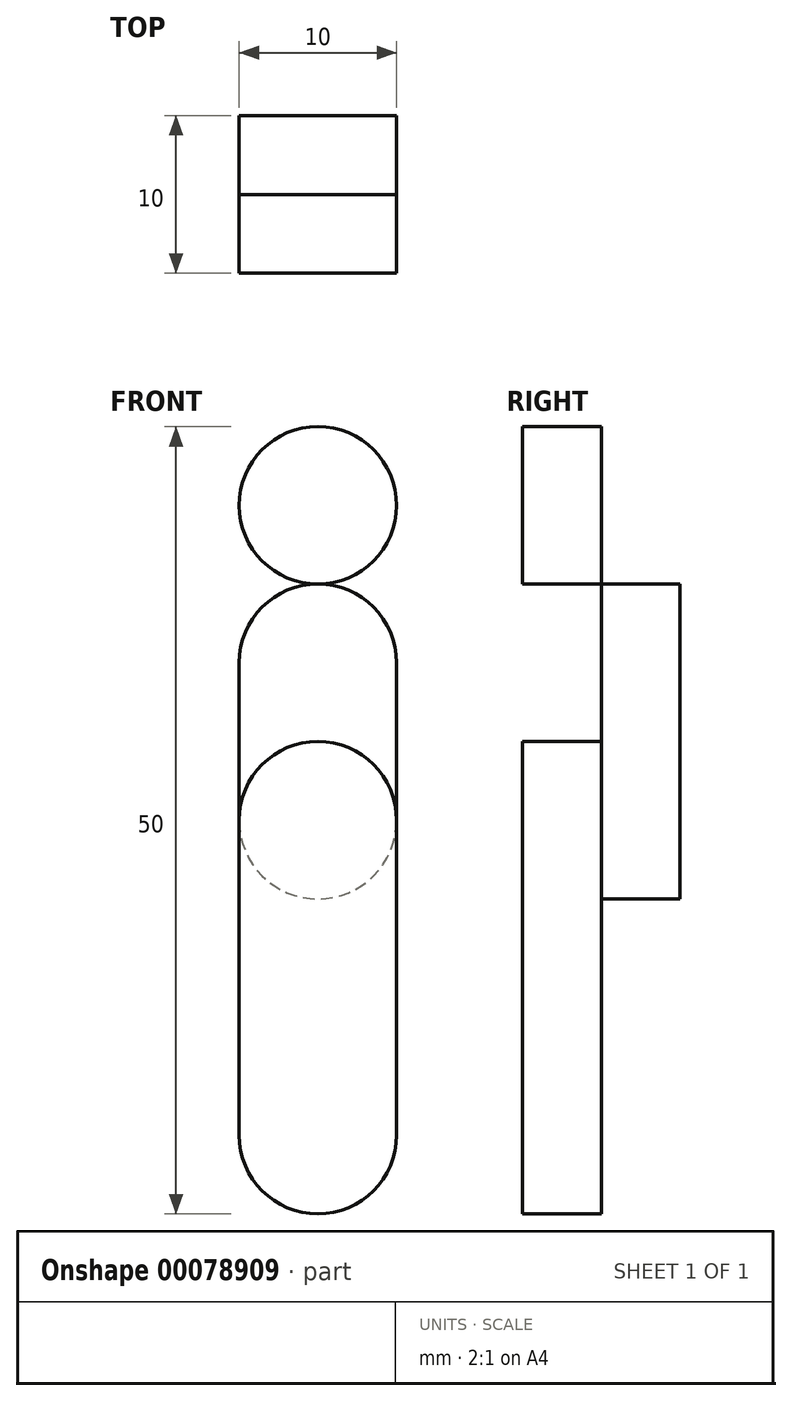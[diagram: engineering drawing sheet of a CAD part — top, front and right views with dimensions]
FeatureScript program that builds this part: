
annotation { "Feature Type Name" : "Feature", "Feature Type Description" : "" }
export const myFeature = defineFeature(function(context is Context, id is Id, definition is map)
    precondition{}
    {
        {
            var Q0;
            Q0=qCreatedBy(makeId("Front.planeOp"),FACE);
            var sketch = newSketch(context, id + "F0", { "sketchPlane" : qUnion([Q0])});
            skArc(sketch, "E0", {"start": v(10, 0) * mm, "mid": v(5, 5) * mm, "end": v(0, 0) * mm});
            skLineSegment(sketch, "E1", {"start": v(10, 0) * mm, "end": v(10, -20) * mm});
            skLineSegment(sketch, "E2", {"start": v(0, 0) * mm, "end": v(0, -20) * mm});
            skArc(sketch, "E3", {"start": v(0, -20) * mm, "mid": v(5, -25) * mm, "end": v(10, -20) * mm});
            skCircle(sketch, "E4", {"center": v(5, -10) * mm, "radius": 5 * mm});
            skLineSegment(sketch, "E5", {"start": v(0, 0) * mm, "end": v(10, -20) * mm, "construction": true});
            skLineSegment(sketch, "E6", {"start": v(10, 0) * mm, "end": v(0, -20) * mm, "construction": true});
            skCircle(sketch, "E7", {"center": v(5, 0) * mm, "radius": 5 * mm});
            skCircle(sketch, "E8", {"center": v(5, -20) * mm, "radius": 5 * mm});
            skArc(sketch, "E9", {"start": v(10, 30) * mm, "mid": v(5, 35) * mm, "end": v(0, 30) * mm});
            skLineSegment(sketch, "E10", {"start": v(10, 30) * mm, "end": v(10, 10) * mm});
            skLineSegment(sketch, "E11", {"start": v(0, 30) * mm, "end": v(0, 10) * mm});
            skArc(sketch, "E12", {"start": v(0, 10) * mm, "mid": v(5, 5) * mm, "end": v(10, 10) * mm});
            skCircle(sketch, "E13", {"center": v(5, 20) * mm, "radius": 5 * mm});
            skLineSegment(sketch, "E14", {"start": v(0, 30) * mm, "end": v(10, 10) * mm, "construction": true});
            skLineSegment(sketch, "E15", {"start": v(10, 30) * mm, "end": v(0, 10) * mm, "construction": true});
            skCircle(sketch, "E16", {"center": v(5, 30) * mm, "radius": 5 * mm});
            skCircle(sketch, "E17", {"center": v(5, 10) * mm, "radius": 5 * mm});
            skLineSegment(sketch, "E18", {"start": v(0, 10) * mm, "end": v(0, 0) * mm});
            skLineSegment(sketch, "E19", {"start": v(10, 0) * mm, "end": v(10, 10) * mm});
            skSolve(sketch);
        }
        {
            var Q0;
            {var subQ0=sQuery(id+"F0.wireOp",EDGE,"E7");var subQ2=makeQuery(id+"F0.imprint","INTERSECT",VERTEX,{"derivedFrom":[subQ0,sQuery(id+"F0.wireOp",EDGE,"E17")]});Q0=makeQuery(id+"F0.imprint","IMPRINT",FACE,{"disambiguationData":[TD([[makeQuery(id+"F0.imprint","IMPRINT",EDGE,{"disambiguationData":[TD([[subQ2,1.0]])],"derivedFrom":subQ0}),1.0]])]});}
            var Q1;
            {var subQ1=sQuery(id+"F0.wireOp",EDGE,"E2");var subQ3=sQuery(id+"F0.wireOp",EDGE,"E4");var subQ4=makeQuery(id+"F0.imprint","INTERSECT",VERTEX,{"derivedFrom":[subQ1,subQ3]});Q1=makeQuery(id+"F0.imprint","IMPRINT",FACE,{"disambiguationData":[TD([[makeQuery(id+"F0.imprint","IMPRINT",EDGE,{"disambiguationData":[TD([[subQ4,1.0]])],"derivedFrom":subQ3}),-1.0]])]});}
            var Q2;
            {var subQ0=sQuery(id+"F0.wireOp",EDGE,"E4");var subQ1=makeQuery(id+"F0.imprint","INTERSECT",VERTEX,{"derivedFrom":[sQuery(id+"F0.wireOp",EDGE,"E1"),subQ0]});Q2=makeQuery(id+"F0.imprint","IMPRINT",FACE,{"disambiguationData":[TD([[makeQuery(id+"F0.imprint","IMPRINT",EDGE,{"disambiguationData":[TD([[subQ1,-1.0]])],"derivedFrom":subQ0}),1.0]])]});}
            var Q3;
            {var subQ0=sQuery(id+"F0.wireOp",EDGE,"E8");var subQ1=sQuery(id+"F0.wireOp",EDGE,"E2");var subQ2=makeQuery(id+"F0.imprint","INTERSECT",VERTEX,{"derivedFrom":[subQ1,subQ0]});Q3=makeQuery(id+"F0.imprint","IMPRINT",FACE,{"disambiguationData":[TD([[makeQuery(id+"F0.imprint","IMPRINT",EDGE,{"disambiguationData":[TD([[subQ2,1.0]])],"derivedFrom":subQ1}),1.0]])]});}
            var Q4;
            {var subQ0=sQuery(id+"F0.wireOp",EDGE,"E8");var subQ1=makeQuery(id+"F0.imprint","INTERSECT",VERTEX,{"derivedFrom":[sQuery(id+"F0.wireOp",EDGE,"E1"),subQ0]});Q4=makeQuery(id+"F0.imprint","IMPRINT",FACE,{"disambiguationData":[TD([[makeQuery(id+"F0.imprint","IMPRINT",EDGE,{"disambiguationData":[TD([[subQ1,-1.0]])],"derivedFrom":subQ0}),1.0]])]});}
            var Q5;
            {var subQ0=sQuery(id+"F0.wireOp",EDGE,"E8");var subQ1=sQuery(id+"F0.wireOp",EDGE,"E1");var subQ2=makeQuery(id+"F0.imprint","INTERSECT",VERTEX,{"derivedFrom":[subQ1,subQ0]});Q5=makeQuery(id+"F0.imprint","IMPRINT",FACE,{"disambiguationData":[TD([[makeQuery(id+"F0.imprint","IMPRINT",EDGE,{"disambiguationData":[TD([[subQ2,1.0]])],"derivedFrom":subQ1}),-1.0]])]});}
            var Q6;
            {var subQ1=sQuery(id+"F0.wireOp",EDGE,"E1");var subQ3=sQuery(id+"F0.wireOp",EDGE,"E4");var subQ4=makeQuery(id+"F0.imprint","INTERSECT",VERTEX,{"derivedFrom":[subQ1,subQ3]});Q6=makeQuery(id+"F0.imprint","IMPRINT",FACE,{"disambiguationData":[TD([[makeQuery(id+"F0.imprint","IMPRINT",EDGE,{"disambiguationData":[TD([[subQ4,-1.0]])],"derivedFrom":subQ3}),-1.0]])]});}
            extrude(context, id + "F1", {"entities" : qUnion([Q0, Q1, Q2, Q3, Q4, Q5, Q6]), "depth" : 5 * mm});
        }
        {
            var Q0;
            {var subQ0=sQuery(id+"F0.wireOp",EDGE,"E7");var subQ2=makeQuery(id+"F0.imprint","INTERSECT",VERTEX,{"derivedFrom":[subQ0,sQuery(id+"F0.wireOp",EDGE,"E17")]});Q0=makeQuery(id+"F0.imprint","IMPRINT",FACE,{"disambiguationData":[TD([[makeQuery(id+"F0.imprint","IMPRINT",EDGE,{"disambiguationData":[TD([[subQ2,1.0]])],"derivedFrom":subQ0}),1.0]])]});}
            var Q1;
            {var subQ0=sQuery(id+"F0.wireOp",EDGE,"E18");Q1=makeQuery(id+"F0.imprint","IMPRINT",FACE,{"disambiguationData":[TD([[makeQuery(id+"F0.imprint","IMPRINT",EDGE,{"derivedFrom":subQ0}),1.0]])]});}
            var Q2;
            {var subQ0=sQuery(id+"F0.wireOp",EDGE,"E19");Q2=makeQuery(id+"F0.imprint","IMPRINT",FACE,{"disambiguationData":[TD([[makeQuery(id+"F0.imprint","IMPRINT",EDGE,{"derivedFrom":subQ0}),1.0]])]});}
            var Q3;
            {var subQ0=sQuery(id+"F0.wireOp",EDGE,"E17");var subQ2=makeQuery(id+"F0.imprint","INTERSECT",VERTEX,{"derivedFrom":[sQuery(id+"F0.wireOp",EDGE,"E13"),subQ0]});Q3=makeQuery(id+"F0.imprint","IMPRINT",FACE,{"disambiguationData":[TD([[makeQuery(id+"F0.imprint","IMPRINT",EDGE,{"disambiguationData":[TD([[subQ2,1.0]])],"derivedFrom":subQ0}),1.0]])]});}
            extrude(context, id + "F2", {"entities" : qUnion([Q0, Q1, Q2, Q3]), "oppositeDirection" : true, "depth" : 5 * mm});
        }
        {
            var Q0;
            {var subQ0=sQuery(id+"F0.wireOp",EDGE,"E13");var subQ1=makeQuery(id+"F0.imprint","INTERSECT",VERTEX,{"derivedFrom":[sQuery(id+"F0.wireOp",EDGE,"E10"),subQ0]});Q0=makeQuery(id+"F0.imprint","IMPRINT",FACE,{"disambiguationData":[TD([[makeQuery(id+"F0.imprint","IMPRINT",EDGE,{"disambiguationData":[TD([[subQ1,-1.0]])],"derivedFrom":subQ0}),1.0]])]});}
            extrude(context, id + "F3", {"entities" : qUnion([Q0]), "depth" : 5 * mm});
        }
    });
